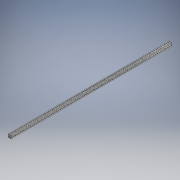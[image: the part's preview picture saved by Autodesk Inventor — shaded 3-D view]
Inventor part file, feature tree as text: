
AUTODESK INVENTOR PART (.ipt)
format: ipt  version: 2022 (Build 260153000, 153)  size: 176,128 bytes
history: native  units: mm
features: extrude x1, sketch x1
ambient origin geometry x8: Origin, YZ Plane, XZ Plane, XY Plane, X Axis, Y Axis, Z Axis, Center Point
bodies: Solid1 (feature_tree)
feature tree (2):
  extrude  "Extrusion1"  [1 undecoded]
  sketch  "Sketch1"  dims[d0=1000.0mm d1=0.0mm]
note: 1 required parameter value undecoded (feature->parameter linkage not recoverable at this tier; creation-order binding heuristic only, values carry confidence <= 0.55)
